# Revit family: Haworth_CabanaLounge_Half-BackSofa_Retreat_AP_PRELIMINARY
name_source: partatom
category: Furniture
revit_build: Autodesk Revit 2018 (Build: 20170223_1515(x64)
units: mm (PartAtom-declared; Revit-internal decimal feet)

## family parameters
Always vertical = Yes
Cut with Voids When Loaded = No
OmniClass Number = 23.40.70.14.64.21
OmniClass Title = Systems Furniture
Room Calculation Point = No
Shared = No
Work Plane-Based = No

## types (8) — shared parameters
Actual Depth = 813 mm
Actual Width = 2642 mm  [stored 8.66798 ft]
Assembly Code = E2020200
Back Width = 1067 mm  [stored 3.50066 ft]
Description = Haworth - Cabana Lounge - Half Back Sofa - Retreat
Leg Offset = 70 mm  [stored 0.229659 ft]
Manufacturer = Haworth
Model = SECBFR
Rectangle Control = No
Revision Number = 1
Screen Width = 1880 mm  [stored 6.16798 ft]
Seat Depth = 762 mm
Seat Height = 459 mm  [stored 1.50591 ft]
Seat Width = 1829 mm  [stored 6.00066 ft]
Size = Verify Final Dim. w/ Haworth
Square Control = Yes
Table Width = 762 mm
URL = https://www.haworth.com
URL - Product = https://www.haworth.com
Warranty = http://www.haworth.com

## per-type parameters (varying)
| type | Actual Height | High Screen | Low Screen | Tiered Top | With Top |
| High Screen - With Integrated Table - With Tiered Top | 1372 mm  [stored 4.50131 ft] | Yes | No | Yes | Yes |
| High Screen - With Integrated Table - Without Tiered Top | 1372 mm  [stored 4.50131 ft] | Yes | No | No | Yes |
| High Screen - Without Integrated Table - Without Tiered Top | 1372 mm  [stored 4.50131 ft] | Yes | No | No | No |
| Low Screen - With Integrated Table - With Tiered Top | 1067 mm  [stored 3.50066 ft] | No | Yes | Yes | Yes |
| Low Screen - With Integrated Table - Without Tiered Top | 1067 mm  [stored 3.50066 ft] | No | Yes | No | Yes |
| Low Screen - Without Integrated Table - Without Tiered Top | 1067 mm  [stored 3.50066 ft] | No | Yes | No | No |
| High Screen - Without Integrated Table - With Tiered Top | 1372 mm  [stored 4.50131 ft] | Yes | No | Yes | No |
| Low Screen - Without Integrated Table - With Tiered Top | 1067 mm  [stored 3.50066 ft] | No | Yes | Yes | No |

note: [stored X ft] marks values corroborated as IEEE doubles in the binary element streams (Revit-internal decimal feet)

## geometry (parser evidence)
native form markers: Extrusion x6, Sweep x18
no freeform markers — native parametric forms only
